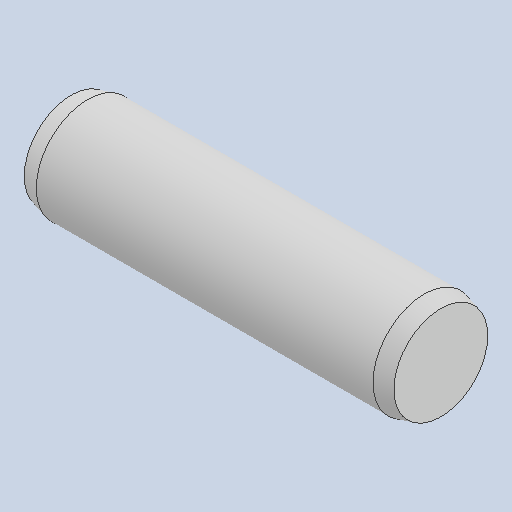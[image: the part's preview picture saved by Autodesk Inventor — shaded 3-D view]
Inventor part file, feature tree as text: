
AUTODESK INVENTOR PART (.ipt)
format: ipt  version: 2022 (Build 260153000, 153)  size: 99,328 bytes
history: native  units: in
note: dims shown in document units (in); Inventor stores cm internally (conversion verified against a paired STEP export)
features: extrude x1
ambient origin geometry x8: Origin, YZ Plane, XZ Plane, XY Plane, X Axis, Y Axis, Z Axis, Center Point
bodies: Solid1 (feature_tree)
feature tree (1):
  extrude  "Extrude3"  [1 undecoded]
note: 1 required parameter value undecoded (feature->parameter linkage not recoverable at this tier; creation-order binding heuristic only, values carry confidence <= 0.55)
